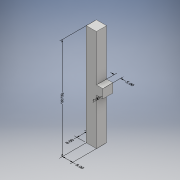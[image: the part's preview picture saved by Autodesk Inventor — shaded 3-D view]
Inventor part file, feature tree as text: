
AUTODESK INVENTOR PART (.ipt)
format: ipt  version: 2018 (Build 220112000, 112)  size: 156,672 bytes
history: native  units: mm
features: other x6, fillet x4, extrude x2, sketch x1
ambient origin geometry x8: Origin, YZ Plane, XZ Plane, XY Plane, X Axis, Y Axis, Z Axis, Center Point
bodies: Solide1 (feature_tree)
feature tree (13):
  other  "Annotations"
  extrude  "Extrusion1"  Depth=40.0mm
  extrude  "Extrusion2"  Depth=40.0mm
  fillet  "Congé1"  Radius=8.0mm
  fillet  "Congé2"  Radius=8.0mm
  fillet  "Congé3"  Radius=3.5mm
  fillet  "Congé4"  Radius=3.5mm
  sketch  "Esquisse1"
  other  "Cote linéaire 1"
  other  "Cote linéaire 2"
  other  "Cote linéaire 3"
  other  "Cote linéaire 4"
  other  "Cote linéaire 5"
